# Revit family: BC_Hitachi_CH-BOX-CH-AP16MSSX_LOD200
name_source: partatom
category: Equipement de génie climatique
revit_build: Autodesk Revit 2015 (Build: 20140606_1530(x64)
units: mm (PartAtom-declared; Revit-internal decimal feet)

## types (1)
- CH-AP16MSSX
    CALC_BOX Width = 303 mm
    CALC_Refrigerant Gas Diameter = 20.4 mm  [stored 0.0669291 ft]
    CALC_Refrigerant Gas HL Left = 200 mm  [stored 0.656168 ft]
    CALC_Refrigerant Gas High_Low Pressure Diameter = 36.08 mm  [stored 0.118373 ft]
    CALC_Refrigerant Gas L Left = 250 mm  [stored 0.82021 ft]
    CALC_Refrigerant Gas Low Pressure Diameter = 33.1 mm  [stored 0.108596 ft]
    CALC_Refrigerant Gas Right = 89 mm  [stored 0.291995 ft]
    Commentaires du type = CH-AP16MSSX
    Description = Multi CH-Box 16 branches
    Fabricant = Hitachi
    Gas Diameter = 28.58 mm  [stored 0.0937664 ft]
    Mass = 47.00 kg
    Material Box = Par défaut
    Material Connector = Par défaut
    Material Pipe = Par défaut
    Modèle = Multi CH-Box
    Nominal Voltage = 230 V
    Overall Depth = 352 mm  [stored 1.15486 ft]
    Overall Height = 260 mm  [stored 0.853018 ft]
    Overall Width = 1060 mm  [stored 3.47769 ft]
    Product Code = 60292163
    Rated Frequency (Hz) = 50
    Refrigerant Gas Low Pressure Diameter = 25.6 mm  [stored 0.0839895 ft]
    Refrigerant Gas Pipe connections Diameter = 15.88 mm  [stored 0.0520997 ft]
    Refrigerant Liquid Diameter = 12.9 mm  [stored 0.0423228 ft]
    Refrigerant Liquid Pipe connections Diameter = 9.52 mm

note: [stored X ft] marks values corroborated as IEEE doubles in the binary element streams (Revit-internal decimal feet)
